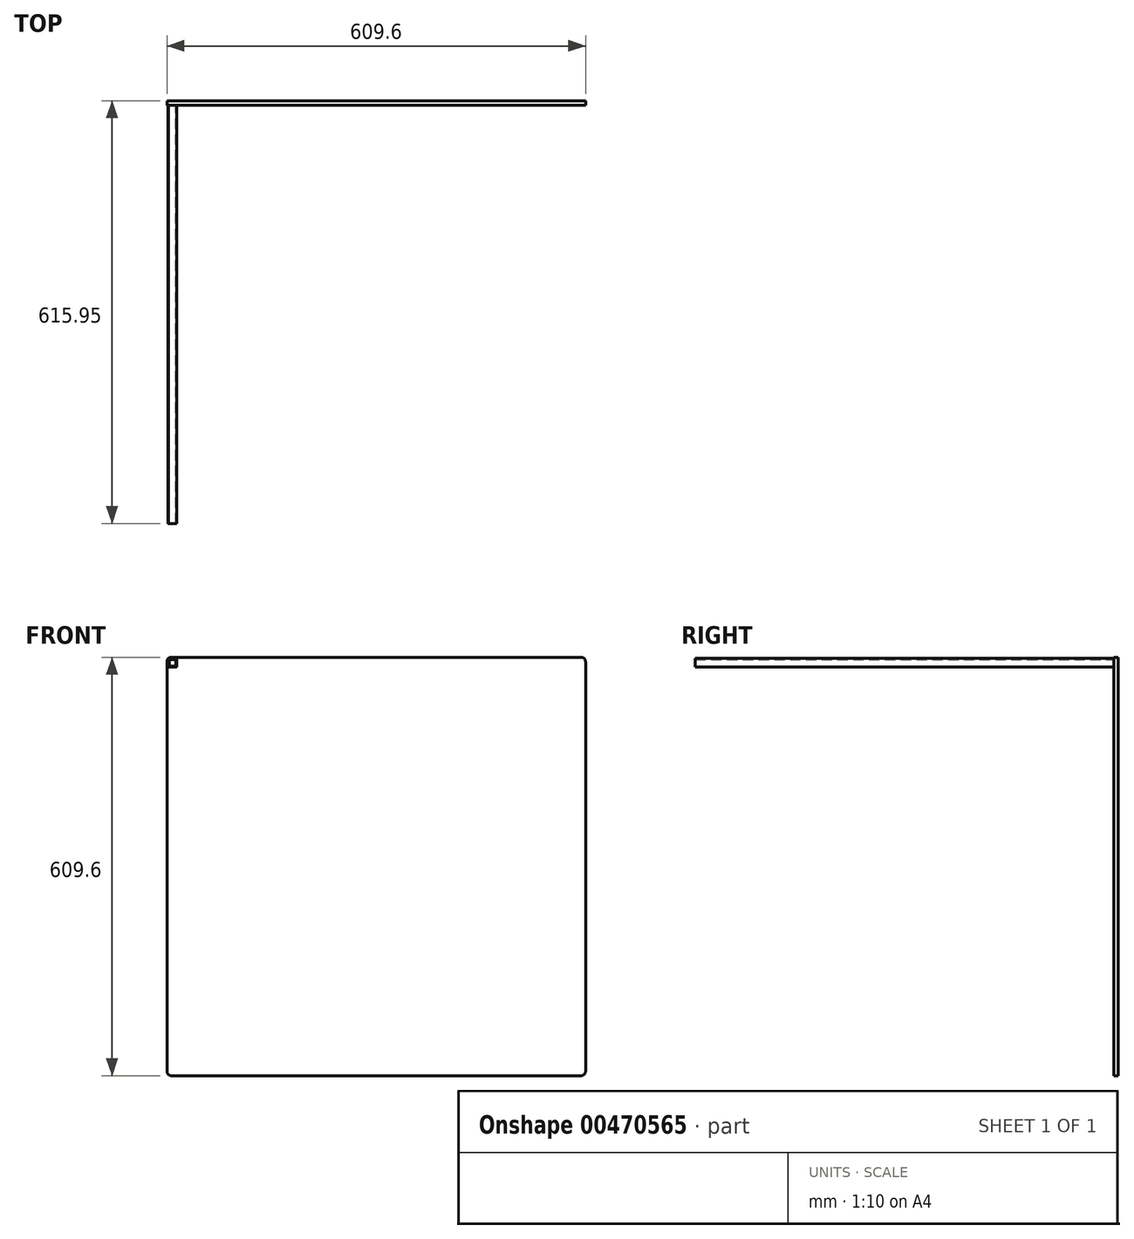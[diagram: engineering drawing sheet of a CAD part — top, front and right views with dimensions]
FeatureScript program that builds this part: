
annotation { "Feature Type Name" : "Feature", "Feature Type Description" : "" }
export const myFeature = defineFeature(function(context is Context, id is Id, definition is map)
    precondition{}
    {
        {
            var Q0;
            Q0=qCreatedBy(makeId("Front.planeOp"),FACE);
            var sketch = newSketch(context, id + "F0", { "sketchPlane" : qUnion([Q0])});
            skLineSegment(sketch, "E0.bottom", {"start": v(298.45, -304.8) * mm, "end": v(-298.45, -304.8) * mm});
            skLineSegment(sketch, "E0.top", {"start": v(298.45, 304.8) * mm, "end": v(-298.45, 304.8) * mm});
            skLineSegment(sketch, "E0.left", {"start": v(304.8, -298.45) * mm, "end": v(304.8, 298.45) * mm});
            skLineSegment(sketch, "E0.right", {"start": v(-304.8, -298.45) * mm, "end": v(-304.8, 298.45) * mm});
            skPoint(sketch, "E0.middle", {"position": v(0, 0) * mm});
            skPoint(sketch, "E1.visualSharp", {"position": v(-304.8, 304.8) * mm});
            skArc(sketch, "E1.filletArc", {"start": v(-298.45, 304.8) * mm, "mid": v(-302.94, 302.94) * mm, "end": v(-304.8, 298.45) * mm});
            skPoint(sketch, "E2.visualSharp", {"position": v(304.8, 304.8) * mm});
            skArc(sketch, "E2.filletArc", {"start": v(304.8, 298.45) * mm, "mid": v(302.94, 302.94) * mm, "end": v(298.45, 304.8) * mm});
            skPoint(sketch, "E3.visualSharp", {"position": v(304.8, -304.8) * mm});
            skArc(sketch, "E3.filletArc", {"start": v(298.45, -304.8) * mm, "mid": v(302.94, -302.94) * mm, "end": v(304.8, -298.45) * mm});
            skPoint(sketch, "E4.visualSharp", {"position": v(-304.8, -304.8) * mm});
            skArc(sketch, "E4.filletArc", {"start": v(-304.8, -298.45) * mm, "mid": v(-302.94, -302.94) * mm, "end": v(-298.45, -304.8) * mm});
            skSolve(sketch);
        }
        {
            var Q0;
            Q0=makeQuery(id+"F0.imprint","IMPRINT",FACE,{"disambiguationData":[TD([[makeQuery(id+"F0.imprint","IMPRINT",EDGE,{"derivedFrom":sQuery(id+"F0.wireOp",EDGE,"E0.bottom")}),-1.0]])]});
            extrude(context, id + "F1", {"entities" : qUnion([Q0]), "depth" : 6.35 * mm});
        }
        {
            var Q0;
            Q0=makeQuery(id+"F1.opExtrude","CAP_FACE",FACE,{"disambiguationData":[OSD([sQuery(id+"F0.wireOp",EDGE,"E0.bottom"),sQuery(id+"F0.wireOp",EDGE,"E0.top"),sQuery(id+"F0.wireOp",EDGE,"E0.left"),sQuery(id+"F0.wireOp",EDGE,"E0.right"),sQuery(id+"F0.wireOp",EDGE,"E1.filletArc"),sQuery(id+"F0.wireOp",EDGE,"E2.filletArc"),sQuery(id+"F0.wireOp",EDGE,"E3.filletArc"),sQuery(id+"F0.wireOp",EDGE,"E4.filletArc")])],"isStart":false});
            var sketch = newSketch(context, id + "F2", { "sketchPlane" : qUnion([Q0])});
            skLineSegment(sketch, "E5.bottom", {"start": v(-302.39, 303.2) * mm, "end": v(-291.31, 303.2) * mm});
            skLineSegment(sketch, "E5.top", {"start": v(-302.39, 290.5) * mm, "end": v(-291.31, 290.5) * mm});
            skLineSegment(sketch, "E5.left", {"start": v(-303.2, 302.39) * mm, "end": v(-303.2, 291.31) * mm});
            skLineSegment(sketch, "E5.right", {"start": v(-290.5, 302.39) * mm, "end": v(-290.5, 291.31) * mm});
            skPoint(sketch, "E6.visualSharp", {"position": v(-303.2, 303.2) * mm});
            skArc(sketch, "E6.filletArc", {"start": v(-302.39, 303.2) * mm, "mid": v(-302.96, 302.96) * mm, "end": v(-303.2, 302.39) * mm});
            skPoint(sketch, "E7.visualSharp", {"position": v(-303.2, 290.5) * mm});
            skArc(sketch, "E7.filletArc", {"start": v(-303.2, 291.31) * mm, "mid": v(-302.96, 290.74) * mm, "end": v(-302.39, 290.5) * mm});
            skPoint(sketch, "E8.visualSharp", {"position": v(-290.5, 290.5) * mm});
            skArc(sketch, "E8.filletArc", {"start": v(-291.31, 290.5) * mm, "mid": v(-290.74, 290.74) * mm, "end": v(-290.5, 291.31) * mm});
            skPoint(sketch, "E9.visualSharp", {"position": v(-290.5, 303.2) * mm});
            skArc(sketch, "E9.filletArc", {"start": v(-290.5, 302.39) * mm, "mid": v(-290.74, 302.96) * mm, "end": v(-291.31, 303.2) * mm});
            skLineSegment(sketch, "E10.bottom", {"start": v(-300.79, 301.6) * mm, "end": v(-292.91, 301.6) * mm});
            skLineSegment(sketch, "E10.top", {"start": v(-300.79, 292.1) * mm, "end": v(-292.91, 292.1) * mm});
            skLineSegment(sketch, "E10.left", {"start": v(-301.6, 300.79) * mm, "end": v(-301.6, 292.91) * mm});
            skLineSegment(sketch, "E10.right", {"start": v(-292.1, 300.79) * mm, "end": v(-292.1, 292.91) * mm});
            skPoint(sketch, "E11.visualSharp", {"position": v(-301.6, 301.6) * mm});
            skArc(sketch, "E11.filletArc", {"start": v(-300.79, 301.6) * mm, "mid": v(-301.36, 301.36) * mm, "end": v(-301.6, 300.79) * mm});
            skPoint(sketch, "E12.visualSharp", {"position": v(-301.6, 292.1) * mm});
            skArc(sketch, "E12.filletArc", {"start": v(-301.6, 292.91) * mm, "mid": v(-301.36, 292.34) * mm, "end": v(-300.79, 292.1) * mm});
            skPoint(sketch, "E13.visualSharp", {"position": v(-292.1, 292.1) * mm});
            skArc(sketch, "E13.filletArc", {"start": v(-292.91, 292.1) * mm, "mid": v(-292.34, 292.34) * mm, "end": v(-292.1, 292.91) * mm});
            skPoint(sketch, "E14.visualSharp", {"position": v(-292.1, 301.6) * mm});
            skArc(sketch, "E14.filletArc", {"start": v(-292.1, 300.79) * mm, "mid": v(-292.34, 301.36) * mm, "end": v(-292.91, 301.6) * mm});
            skSolve(sketch);
        }
        {
            var Q0;
            {var subQ4=sQuery(id+"F2.wireOp",EDGE,"E5.bottom");Q0=makeQuery(id+"F2.imprint","IMPRINT",FACE,{"disambiguationData":[TD([[makeQuery(id+"F2.imprint","IMPRINT",EDGE,{"derivedFrom":subQ4}),-1.0]])]});}
            extrude(context, id + "F3", {"entities" : qUnion([Q0]), "depth" : 609.6 * mm});
        }
    });
